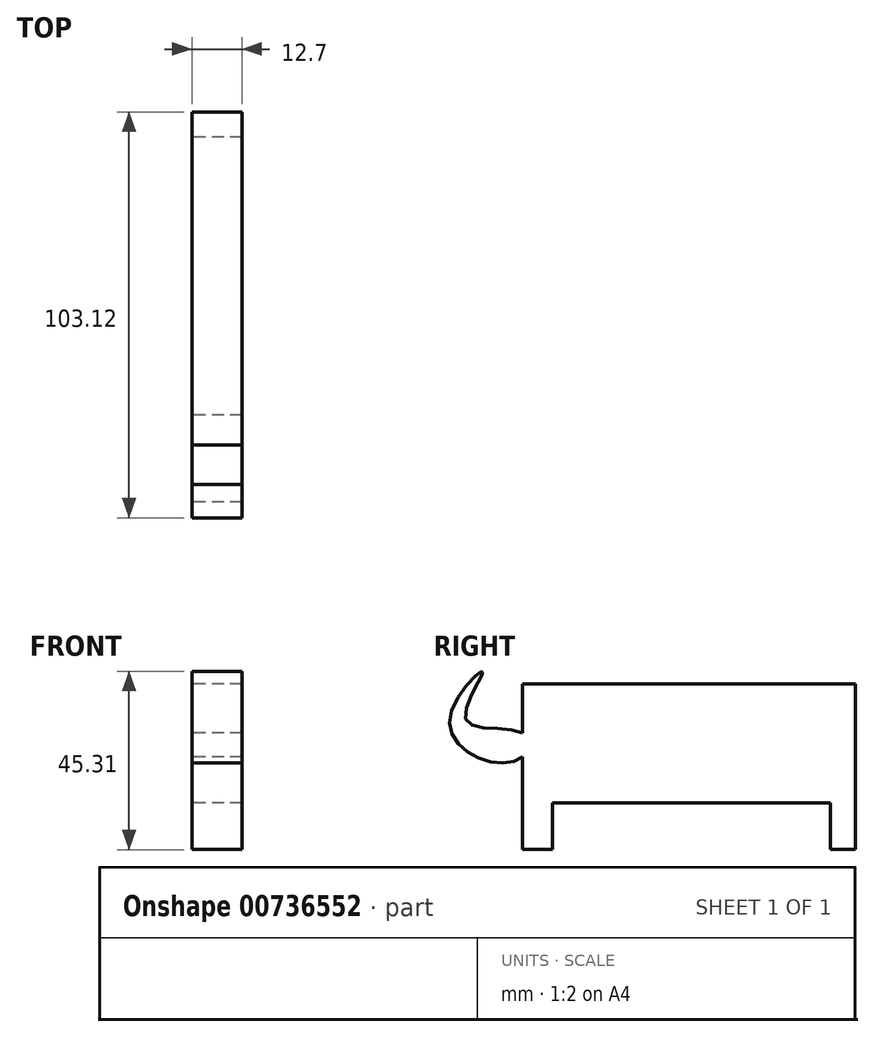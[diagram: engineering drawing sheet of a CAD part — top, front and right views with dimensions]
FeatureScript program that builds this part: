
annotation { "Feature Type Name" : "Feature", "Feature Type Description" : "" }
export const myFeature = defineFeature(function(context is Context, id is Id, definition is map)
    precondition{}
    {
        {
            var Q0;
            Q0=qCreatedBy(makeId("Right.planeOp"),FACE);
            var sketch = newSketch(context, id + "F0", { "sketchPlane" : qUnion([Q0])});
            skLineSegment(sketch, "E0.bottom", {"start": v(42.3, 15.12) * mm, "end": v(-42.3, 15.12) * mm});
            skLineSegment(sketch, "E0.top", {"start": v(42.3, -15.12) * mm, "end": v(-42.3, -15.12) * mm});
            skLineSegment(sketch, "E0.left", {"start": v(42.3, 15.12) * mm, "end": v(42.3, -15.12) * mm});
            skLineSegment(sketch, "E0.right", {"start": v(-42.3, 15.12) * mm, "end": v(-42.3, -15.12) * mm});
            skPoint(sketch, "E0.middle", {"position": v(0, 0) * mm});
            skLineSegment(sketch, "E1.bottom", {"start": v(42.3, -15.12) * mm, "end": v(35.88, -15.12) * mm});
            skLineSegment(sketch, "E1.top", {"start": v(42.3, -27.03) * mm, "end": v(35.88, -27.03) * mm});
            skLineSegment(sketch, "E1.left", {"start": v(42.3, -15.12) * mm, "end": v(42.3, -27.03) * mm});
            skLineSegment(sketch, "E1.right", {"start": v(35.88, -15.12) * mm, "end": v(35.88, -27.03) * mm});
            skLineSegment(sketch, "E2.bottom", {"start": v(-42.3, -15.12) * mm, "end": v(-34.66, -15.12) * mm});
            skLineSegment(sketch, "E2.top", {"start": v(-42.3, -27.03) * mm, "end": v(-34.66, -27.03) * mm});
            skLineSegment(sketch, "E2.left", {"start": v(-42.3, -15.12) * mm, "end": v(-42.3, -27.03) * mm});
            skLineSegment(sketch, "E2.right", {"start": v(-34.66, -15.12) * mm, "end": v(-34.66, -27.03) * mm});
            skFitSpline(sketch, "E3", {"points": [v(-42.3, 2.6) * mm, v(-56.65, 5.95) * mm, v(-52.37, 18.17) * mm, v(-60.31, 8.4) * mm, v(-55.12, -2.9) * mm, v(-42.3, -3.51) * mm, v(-42.3, 2.6) * mm]});
            skSolve(sketch);
        }
        {
            var Q0;
            Q0 = qSketchRegion(id + "F0", true);
            extrude(context, id + "F1", {"entities" : qUnion([Q0]), "depth" : 12.7 * mm, "offsetDistance" : 25.4 * mm});
        }
    });
